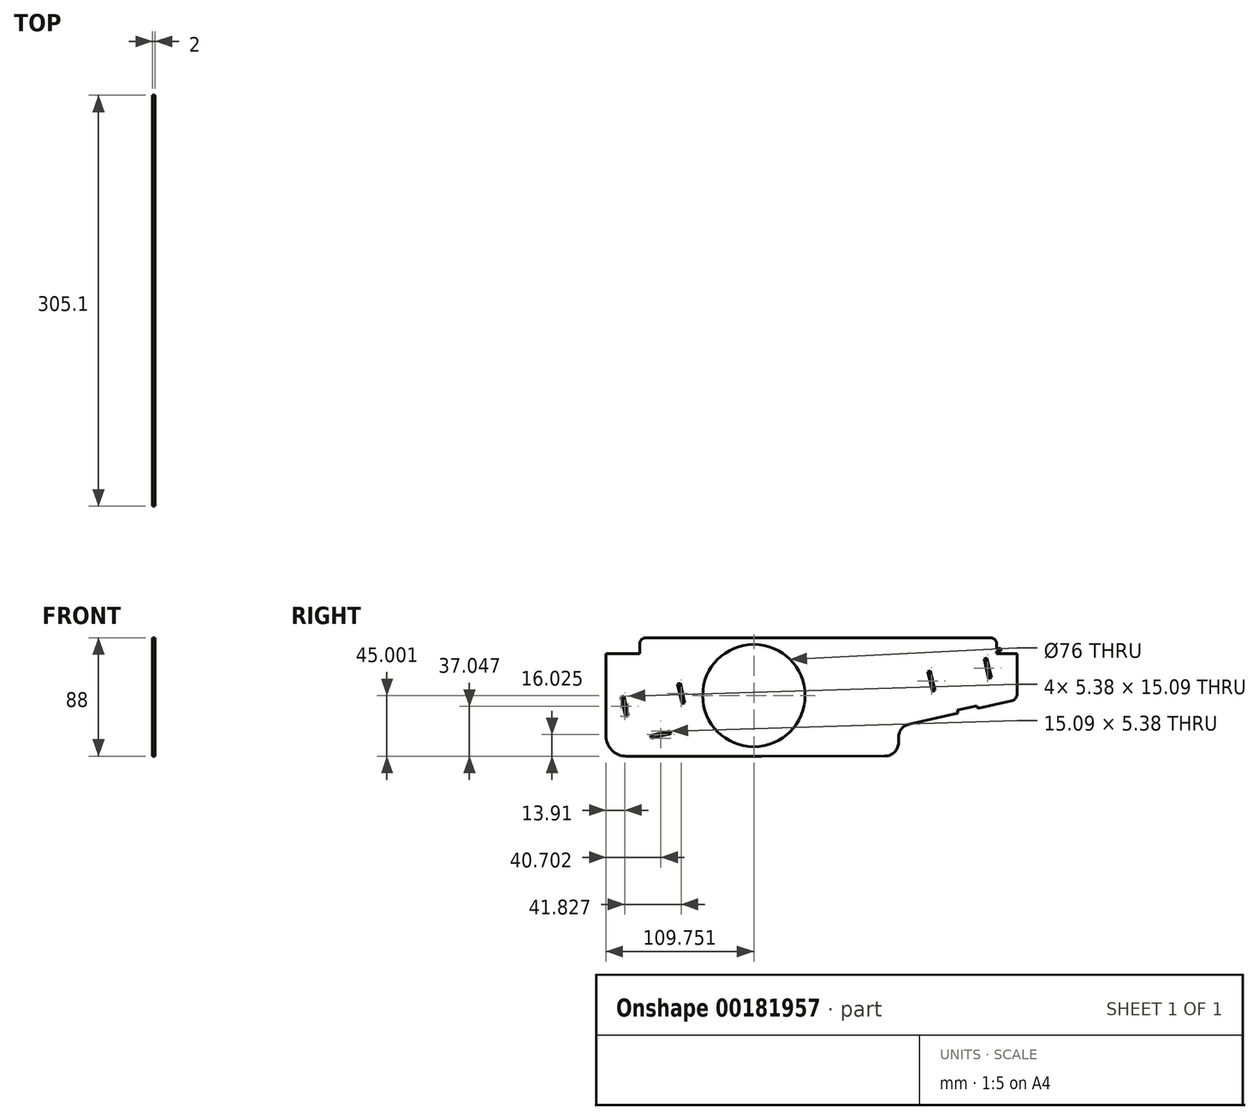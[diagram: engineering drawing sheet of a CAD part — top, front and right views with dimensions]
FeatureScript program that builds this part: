
annotation { "Feature Type Name" : "Feature", "Feature Type Description" : "" }
export const myFeature = defineFeature(function(context is Context, id is Id, definition is map)
    precondition{}
    {
        {
            var Q0;
            Q0=qCreatedBy(makeId("Right.planeOp"),FACE);
            var sketch = newSketch(context, id + "F0", { "sketchPlane" : qUnion([Q0])});
            skLineSegment(sketch, "E0.bottom", {"start": v(-149.68, 55.67) * mm, "end": v(-146.68, 55.67) * mm});
            skLineSegment(sketch, "E0.top", {"start": v(-156.68, -24.33) * mm, "end": v(-56.2, -24.33) * mm});
            skLineSegment(sketch, "E0.left", {"start": v(-171.68, 51.67) * mm, "end": v(-171.68, -9.33) * mm});
            skPoint(sketch, "E1.visualSharp", {"position": v(-171.68, -24.33) * mm});
            skArc(sketch, "E1.filletArc", {"start": v(-171.68, -9.33) * mm, "mid": v(-167.29, -19.94) * mm, "end": v(-156.68, -24.33) * mm});
            skLineSegment(sketch, "E2", {"start": v(-152.68, -14.33) * mm, "end": v(-108.8, -4.33) * mm});
            skLineSegment(sketch, "E3", {"start": v(-152.68, -14.33) * mm, "end": v(-154.02, -8.48) * mm});
            skLineSegment(sketch, "E4", {"start": v(-110.14, 1.52) * mm, "end": v(-108.8, -4.33) * mm});
            skLineSegment(sketch, "E5", {"start": v(-110.14, 1.52) * mm, "end": v(-116.59, 29.8) * mm});
            skLineSegment(sketch, "E6", {"start": v(-154.02, -8.48) * mm, "end": v(-160.46, 19.8) * mm});
            skLineSegment(sketch, "E7", {"start": v(-138.06, -11) * mm, "end": v(-138.52, -8.95) * mm});
            skLineSegment(sketch, "E8", {"start": v(-138.52, -8.95) * mm, "end": v(-123.9, -5.61) * mm});
            skLineSegment(sketch, "E9", {"start": v(-123.9, -5.61) * mm, "end": v(-123.43, -7.66) * mm});
            skCircle(sketch, "E10", {"center": v(-61.93, 20.67) * mm, "radius": 38 * mm});
            skLineSegment(sketch, "E11.trimOffspring", {"start": v(118.32, 55.67) * mm, "end": v(121.32, 55.67) * mm});
            skLineSegment(sketch, "E12", {"start": v(-146.68, 55.67) * mm, "end": v(-146.68, 58.67) * mm});
            skLineSegment(sketch, "E13", {"start": v(-141.68, 63.67) * mm, "end": v(113.32, 63.67) * mm});
            skLineSegment(sketch, "E14", {"start": v(118.32, 58.67) * mm, "end": v(118.32, 55.67) * mm});
            skPoint(sketch, "E15.visualSharp", {"position": v(-146.68, 63.67) * mm});
            skArc(sketch, "E15.filletArc", {"start": v(-141.68, 63.67) * mm, "mid": v(-145.22, 62.2) * mm, "end": v(-146.68, 58.67) * mm});
            skPoint(sketch, "E16.visualSharp", {"position": v(118.32, 63.67) * mm});
            skArc(sketch, "E16.filletArc", {"start": v(118.32, 58.67) * mm, "mid": v(116.85, 62.2) * mm, "end": v(113.32, 63.67) * mm});
            skLineSegment(sketch, "E17", {"start": v(74.88, 4.37) * mm, "end": v(89.5, 7.7) * mm});
            skLineSegment(sketch, "E18", {"start": v(89.5, 7.7) * mm, "end": v(89.03, 9.75) * mm});
            skLineSegment(sketch, "E19", {"start": v(89.03, 9.75) * mm, "end": v(103.66, 13.09) * mm});
            skLineSegment(sketch, "E20", {"start": v(103.66, 13.09) * mm, "end": v(104.13, 11.04) * mm});
            skLineSegment(sketch, "E21", {"start": v(74.88, 4.37) * mm, "end": v(67.1, 38.5) * mm});
            skLineSegment(sketch, "E22", {"start": v(118.75, 14.37) * mm, "end": v(110.97, 48.5) * mm});
            skLineSegment(sketch, "E23", {"start": v(67.1, 38.5) * mm, "end": v(69.15, 38.96) * mm});
            skLineSegment(sketch, "E24", {"start": v(69.15, 38.96) * mm, "end": v(72.48, 24.34) * mm});
            skLineSegment(sketch, "E25", {"start": v(72.48, 24.34) * mm, "end": v(70.43, 23.87) * mm});
            skLineSegment(sketch, "E26", {"start": v(112.26, 33.4) * mm, "end": v(114.3, 33.87) * mm});
            skLineSegment(sketch, "E27", {"start": v(133.42, 51.67) * mm, "end": v(118.32, 51.67) * mm});
            skLineSegment(sketch, "E28", {"start": v(118.32, 51.67) * mm, "end": v(118.32, 55.67) * mm});
            skLineSegment(sketch, "E29", {"start": v(133.42, 51.67) * mm, "end": v(133.42, 21.7) * mm});
            skLineSegment(sketch, "E30", {"start": v(118.32, 53.67) * mm, "end": v(121.32, 53.67) * mm});
            skLineSegment(sketch, "E31", {"start": v(121.32, 53.67) * mm, "end": v(121.32, 55.67) * mm});
            skLineSegment(sketch, "E32", {"start": v(112.26, 33.4) * mm, "end": v(108.93, 48.03) * mm});
            skLineSegment(sketch, "E33", {"start": v(108.93, 48.03) * mm, "end": v(110.97, 48.5) * mm});
            skLineSegment(sketch, "E34", {"start": v(-160.46, 19.8) * mm, "end": v(-158.41, 20.26) * mm});
            skLineSegment(sketch, "E35", {"start": v(-158.41, 20.26) * mm, "end": v(-155.08, 5.64) * mm});
            skLineSegment(sketch, "E36", {"start": v(-155.08, 5.64) * mm, "end": v(-157.13, 5.17) * mm});
            skLineSegment(sketch, "E37", {"start": v(-116.59, 29.8) * mm, "end": v(-118.63, 29.33) * mm});
            skLineSegment(sketch, "E38", {"start": v(-118.63, 29.33) * mm, "end": v(-115.3, 14.7) * mm});
            skLineSegment(sketch, "E39", {"start": v(-115.3, 14.7) * mm, "end": v(-113.25, 15.17) * mm});
            skLineSegment(sketch, "E40", {"start": v(118.75, 14.37) * mm, "end": v(129.53, 16.83) * mm});
            skLineSegment(sketch, "E41", {"start": v(74.88, 4.37) * mm, "end": v(53.19, -0.57) * mm});
            skPoint(sketch, "E42.start.orphan", {"position": v(77.54, -7.33) * mm});
            skLineSegment(sketch, "E43.trimOffspring", {"start": v(104.13, 11.04) * mm, "end": v(118.75, 14.37) * mm});
            skPoint(sketch, "E44.visualSharp", {"position": v(133.42, 17.71) * mm});
            skArc(sketch, "E44.filletArc", {"start": v(129.53, 16.83) * mm, "mid": v(132.33, 18.58) * mm, "end": v(133.42, 21.7) * mm});
            skLineSegment(sketch, "E45", {"start": v(-146.68, 55.67) * mm, "end": v(-146.68, 51.67) * mm});
            skLineSegment(sketch, "E46", {"start": v(-146.68, 51.67) * mm, "end": v(-171.68, 51.67) * mm});
            skLineSegment(sketch, "E47", {"start": v(-149.68, 55.67) * mm, "end": v(-149.68, 53.67) * mm});
            skLineSegment(sketch, "E48", {"start": v(-149.68, 53.67) * mm, "end": v(-146.68, 53.67) * mm});
            skPoint(sketch, "E49.orphan", {"position": v(-171.68, 55.67) * mm});
            skLineSegment(sketch, "E50", {"start": v(-56.2, -24.33) * mm, "end": v(35.42, -24.22) * mm});
            skLineSegment(sketch, "E51", {"start": v(45.41, -14.2) * mm, "end": v(45.4, -10.33) * mm});
            skArc(sketch, "E52.filletArc", {"start": v(53.19, -0.57) * mm, "mid": v(47.59, -4.1) * mm, "end": v(45.4, -10.33) * mm});
            skPoint(sketch, "E53.visualSharp", {"position": v(45.42, -24.2) * mm});
            skArc(sketch, "E53.filletArc", {"start": v(35.42, -24.22) * mm, "mid": v(42.5, -21.28) * mm, "end": v(45.41, -14.2) * mm});
            skPoint(sketch, "E54", {"position": v(130.82, 51.67) * mm});
            skPoint(sketch, "E55", {"position": v(96.35, 11.42) * mm});
            skSolve(sketch);
        }
        {
            var Q0;
            Q0=makeQuery(id+"F0.imprint","IMPRINT",FACE,{"disambiguationData":[TD([[makeQuery(id+"F0.imprint","IMPRINT",EDGE,{"derivedFrom":sQuery(id+"F0.wireOp",EDGE,"E0.top")}),1.0]])]});
            var Q1;
            {var subQ0=sQuery(id+"F0.wireOp",EDGE,"E11.trimOffspring");Q1=makeQuery(id+"F0.imprint","IMPRINT",FACE,{"disambiguationData":[TD([[makeQuery(id+"F0.imprint","IMPRINT",EDGE,{"derivedFrom":subQ0}),-1.0]])]});}
            var Q2;
            {var subQ0=sQuery(id+"F0.wireOp",EDGE,"E0.bottom");Q2=makeQuery(id+"F0.imprint","IMPRINT",FACE,{"disambiguationData":[TD([[makeQuery(id+"F0.imprint","IMPRINT",EDGE,{"derivedFrom":subQ0}),-1.0]])]});}
            var Q3;
            Q3=makeQuery(id+"F0.imprint","IMPRINT",FACE,{"disambiguationData":[TD([[makeQuery(id+"F0.imprint","IMPRINT",EDGE,{"derivedFrom":sQuery(id+"F0.wireOp",EDGE,"E0.left")}),1.0]])]});
            extrude(context, id + "F1", {"entities" : qUnion([Q0, Q1, Q2, Q3]), "depth" : 2 * mm});
        }
    });
